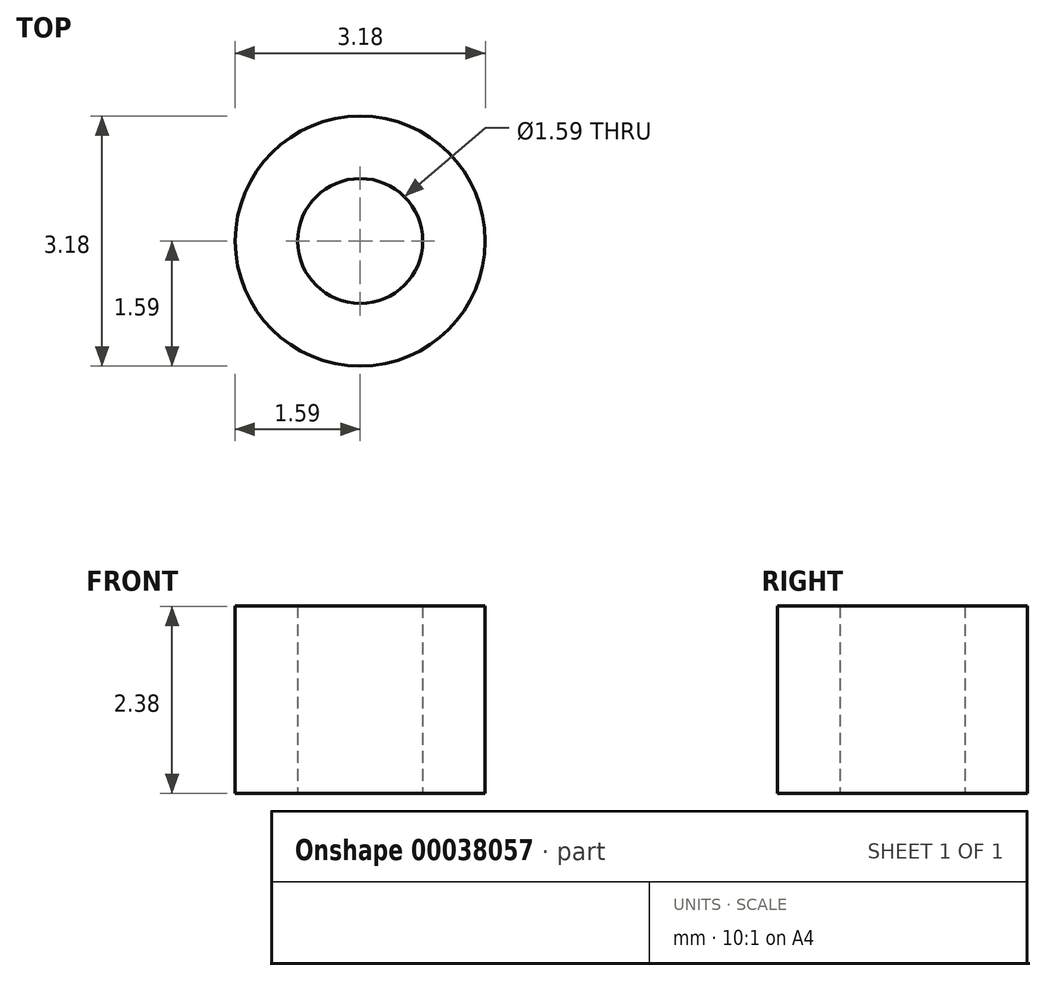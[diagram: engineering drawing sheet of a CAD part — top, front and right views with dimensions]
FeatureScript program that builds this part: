
annotation { "Feature Type Name" : "Feature", "Feature Type Description" : "" }
export const myFeature = defineFeature(function(context is Context, id is Id, definition is map)
    precondition{}
    {
        {
            var Q0;
            Q0=qCreatedBy(makeId("Top.planeOp"),FACE);
            var sketch = newSketch(context, id + "F0", { "sketchPlane" : qUnion([Q0])});
            skCircle(sketch, "E0", {"center": v(0, 0) * mm, "radius": 1.59 * mm});
            skCircle(sketch, "E1", {"center": v(0, 0) * mm, "radius": 0.8 * mm});
            skSolve(sketch);
        }
        {
            var Q0;
            Q0=qSketchRegion(id+"F0",true);
            extrude(context, id + "F1", {"entities" : qUnion([Q0]), "depth" : 2.38 * mm});
        }
    });
